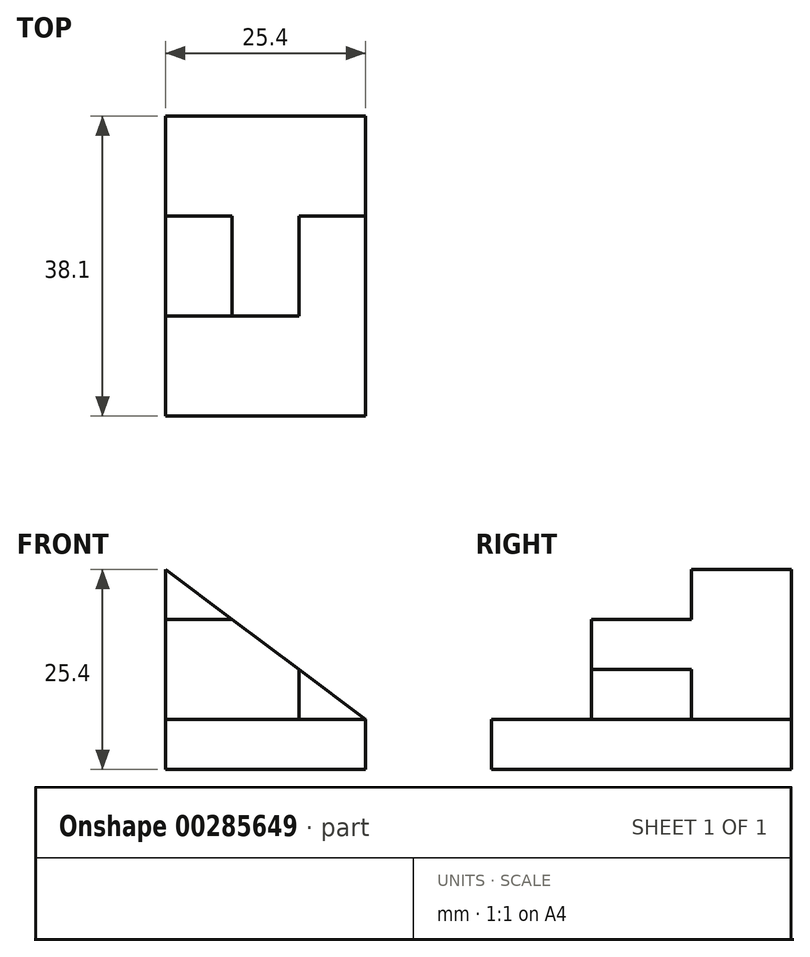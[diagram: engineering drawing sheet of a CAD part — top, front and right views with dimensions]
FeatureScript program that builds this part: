
annotation { "Feature Type Name" : "Feature", "Feature Type Description" : "" }
export const myFeature = defineFeature(function(context is Context, id is Id, definition is map)
    precondition{}
    {
        {
            var Q0;
            Q0=qCreatedBy(makeId("Front.planeOp"),FACE);
            var sketch = newSketch(context, id + "F0", { "sketchPlane" : qUnion([Q0])});
            skLineSegment(sketch, "E0", {"start": v(0, 0) * mm, "end": v(0, 6.35) * mm});
            skLineSegment(sketch, "E1", {"start": v(0, 6.35) * mm, "end": v(25.4, 6.35) * mm});
            skLineSegment(sketch, "E2", {"start": v(25.4, 6.35) * mm, "end": v(25.4, 0) * mm});
            skLineSegment(sketch, "E3", {"start": v(25.4, 0) * mm, "end": v(0, 0) * mm});
            skSolve(sketch);
        }
        {
            var Q0;
            Q0 = qSketchRegion(id + "F0", true);
            extrude(context, id + "F1", {"entities" : qUnion([Q0]), "depth" : 38.1 * mm});
        }
        {
            var Q0;
            Q0=qCreatedBy(makeId("Front.planeOp"),FACE);
            var sketch = newSketch(context, id + "F2", { "sketchPlane" : qUnion([Q0])});
            skLineSegment(sketch, "E4", {"start": v(0, 6.35) * mm, "end": v(0, 19.05) * mm});
            skLineSegment(sketch, "E5", {"start": v(0, 19.05) * mm, "end": v(8.47, 19.05) * mm});
            skLineSegment(sketch, "E6", {"start": v(8.47, 19.05) * mm, "end": v(16.93, 12.7) * mm});
            skLineSegment(sketch, "E7", {"start": v(16.93, 12.7) * mm, "end": v(16.93, 6.35) * mm});
            skLineSegment(sketch, "E8", {"start": v(0, 6.35) * mm, "end": v(16.93, 6.35) * mm});
            skLineSegment(sketch, "E9", {"start": v(0, 25.4) * mm, "end": v(25.4, 6.35) * mm, "construction": true});
            skSolve(sketch);
        }
        {
            var Q0;
            Q0 = qSketchRegion(id + "F2", true);
            extrude(context, id + "F3", {"entities" : qUnion([Q0]), "operationType" : NewBodyOperationType.ADD, "depth" : 25.4 * mm});
        }
        {
            var Q0;
            Q0=qCreatedBy(makeId("Front.planeOp"),FACE);
            var sketch = newSketch(context, id + "F4", { "sketchPlane" : qUnion([Q0])});
            skLineSegment(sketch, "E10", {"start": v(16.93, 12.7) * mm, "end": v(16.93, 6.35) * mm});
            skLineSegment(sketch, "E11", {"start": v(16.93, 6.35) * mm, "end": v(25.4, 6.35) * mm});
            skLineSegment(sketch, "E12", {"start": v(25.4, 6.35) * mm, "end": v(16.93, 12.7) * mm});
            skSolve(sketch);
        }
        {
            var Q0;
            Q0=makeQuery(id+"F4.imprint","IMPRINT",FACE,{"disambiguationData":[TD([[makeQuery(id+"F4.imprint","IMPRINT",EDGE,{"derivedFrom":sQuery(id+"F4.wireOp",EDGE,"E10")}),1.0]])]});
            extrude(context, id + "F5", {"entities" : qUnion([Q0]), "operationType" : NewBodyOperationType.ADD, "depth" : 12.7 * mm});
        }
        {
            var Q0;
            Q0=qCreatedBy(makeId("Front.planeOp"),FACE);
            var sketch = newSketch(context, id + "F6", { "sketchPlane" : qUnion([Q0])});
            skLineSegment(sketch, "E13", {"start": v(0, 19.05) * mm, "end": v(0, 25.4) * mm});
            skLineSegment(sketch, "E14", {"start": v(0, 25.4) * mm, "end": v(8.47, 19.05) * mm});
            skLineSegment(sketch, "E15", {"start": v(8.47, 19.05) * mm, "end": v(0, 19.05) * mm});
            skSolve(sketch);
        }
        {
            var Q0;
            Q0 = qSketchRegion(id + "F6", true);
            extrude(context, id + "F7", {"entities" : qUnion([Q0]), "operationType" : NewBodyOperationType.ADD, "depth" : 12.7 * mm});
        }
    });
